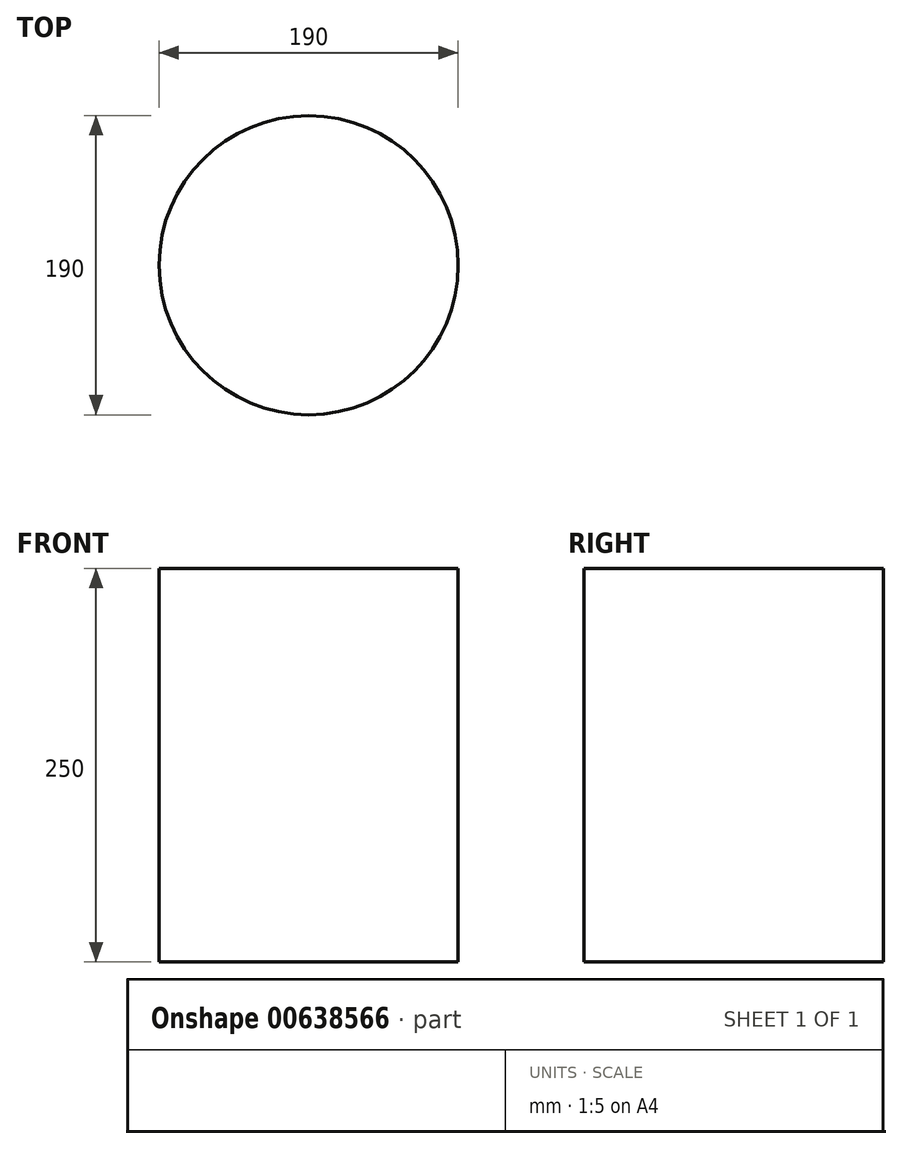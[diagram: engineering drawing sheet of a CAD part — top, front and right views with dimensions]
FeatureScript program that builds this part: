
annotation { "Feature Type Name" : "Feature", "Feature Type Description" : "" }
export const myFeature = defineFeature(function(context is Context, id is Id, definition is map)
    precondition{}
    {
        {
            var Q0;
            Q0=qCreatedBy(makeId("Top.planeOp"),FACE);
            var sketch = newSketch(context, id + "F0", { "sketchPlane" : qUnion([Q0])});
            skCircle(sketch, "E0", {"center": v(0, 0) * mm, "radius": 100 * mm});
            skCircle(sketch, "E1.0", {"center": v(0, 0) * mm, "radius": 95 * mm});
            skSolve(sketch);
        }
        {
            var Q0;
            Q0=makeQuery(id+"F0.imprint","IMPRINT",FACE,{"disambiguationData":[TD([[makeQuery(id+"F0.imprint","IMPRINT",EDGE,{"derivedFrom":sQuery(id+"F0.wireOp",EDGE,"E1.0")}),1.0]])]});
            extrude(context, id + "F1", {"entities" : qUnion([Q0]), "depth" : 250 * mm, "offsetDistance" : 25 * mm});
        }
    });
